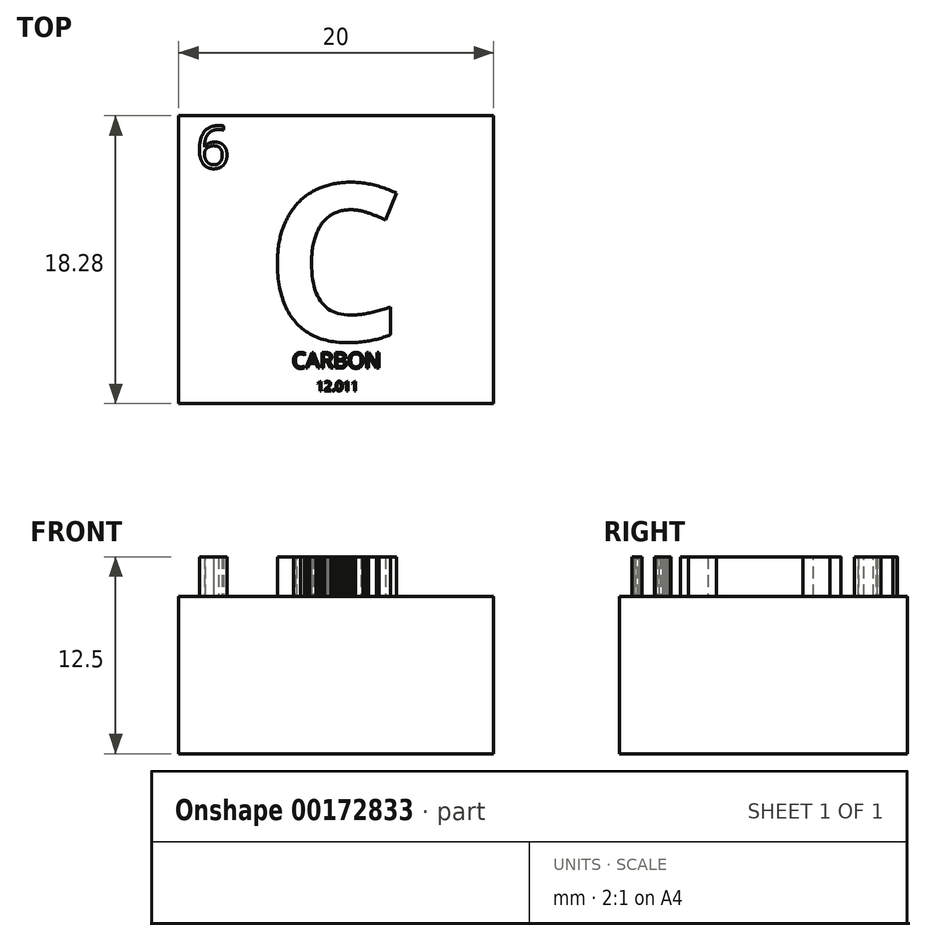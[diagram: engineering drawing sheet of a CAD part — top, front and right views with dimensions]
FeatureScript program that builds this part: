
annotation { "Feature Type Name" : "Feature", "Feature Type Description" : "" }
export const myFeature = defineFeature(function(context is Context, id is Id, definition is map)
    precondition{}
    {
        {
            var Q0;
            Q0=qCreatedBy(makeId("Top.planeOp"),FACE);
            var sketch = newSketch(context, id + "F0", { "sketchPlane" : qUnion([Q0])});
            skLineSegment(sketch, "E0.bottom", {"start": v(-10, 9.14) * mm, "end": v(10, 9.14) * mm});
            skLineSegment(sketch, "E0.top", {"start": v(-10, -9.14) * mm, "end": v(10, -9.14) * mm});
            skLineSegment(sketch, "E0.left", {"start": v(-10, 9.14) * mm, "end": v(-10, -9.14) * mm});
            skLineSegment(sketch, "E0.right", {"start": v(10, 9.14) * mm, "end": v(10, -9.14) * mm});
            skPoint(sketch, "E0.middle", {"position": v(0, 0) * mm});
            skSolve(sketch);
        }
        {
            var Q0;
            Q0 = qSketchRegion(id + "F0", true);
            extrude(context, id + "F1", {"entities" : qUnion([Q0]), "depth" : 10 * mm});
        }
        {
            var Q0;
            Q0=makeQuery(id+"F1.opExtrude","CAP_FACE",FACE,{"disambiguationData":[OSD([sQuery(id+"F0.wireOp",EDGE,"E0.bottom"),sQuery(id+"F0.wireOp",EDGE,"E0.top"),sQuery(id+"F0.wireOp",EDGE,"E0.left"),sQuery(id+"F0.wireOp",EDGE,"E0.right")])],"isStart":false});
            var sketch = newSketch(context, id + "F2", { "sketchPlane" : qUnion([Q0])});
            skText(sketch, "E1", { "text": "C", "fontName": "OpenSans-Bold.ttf"});
            skText(sketch, "E2", { "text": "6\n", "fontName": "OpenSans-Regular.ttf"});
            const initialGuessF2  = {"E1": [-0.00454, -0.00514, 1, 0, 0.01], "E2": [-0.0089, 0.0058, 1, 0, 0.0027]};
            skSetInitialGuess(sketch, initialGuessF2);
            skSolve(sketch);
        }
        {
            var Q0;
            Q0 = qSketchRegion(id + "F2", true);
            var Q1;
            Q1=makeQuery(id+"F1.opExtrude","CAP_FACE",FACE,{"disambiguationData":[OSD([sQuery(id+"F0.wireOp",EDGE,"E0.bottom"),sQuery(id+"F0.wireOp",EDGE,"E0.top"),sQuery(id+"F0.wireOp",EDGE,"E0.left"),sQuery(id+"F0.wireOp",EDGE,"E0.right")])],"isStart":true});
            extrude(context, id + "F3", {"entities" : qUnion([Q0, Q1]), "operationType" : NewBodyOperationType.ADD, "depth" : 2.5 * mm});
        }
        {
            var Q0;
            {var subQ0=sQuery(id+"F0.wireOp",EDGE,"E0.right");var subQ1=sQuery(id+"F0.wireOp",EDGE,"E0.bottom");var subQ2=sQuery(id+"F0.wireOp",EDGE,"E0.left");var subQ3=sQuery(id+"F0.wireOp",EDGE,"E0.top");Q0=makeQuery(id+"F3.boolean.opBoolean","SPLIT",FACE,{"disambiguationData":[TD([makeQuery(id+"F1.opExtrude","SWEPT_FACE",FACE,{"disambiguationData":[OSD([subQ1])]})])],"derivedFrom":makeQuery(id+"F1.opExtrude","CAP_FACE",FACE,{"disambiguationData":[OSD([subQ1,subQ3,subQ2,subQ0])],"isStart":false})});}
            var sketch = newSketch(context, id + "F4", { "sketchPlane" : qUnion([Q0])});
            skText(sketch, "E3", { "text": "CARBON", "fontName": "OpenSans-Regular.ttf"});
            skText(sketch, "E4", { "text": "12.011", "fontName": "OpenSans-Regular.ttf"});
            const initialGuessF4  = {"E3": [-0.0028, -0.0069, 1, 0, 0.001], "E4": [-0.00127, -0.00835, 1, 0, 0.00062]};
            skSetInitialGuess(sketch, initialGuessF4);
            skSolve(sketch);
        }
        {
            var Q0;
            Q0 = qSketchRegion(id + "F4", true);
            extrude(context, id + "F5", {"entities" : qUnion([Q0]), "operationType" : NewBodyOperationType.ADD, "depth" : 2.5 * mm});
        }
    });
